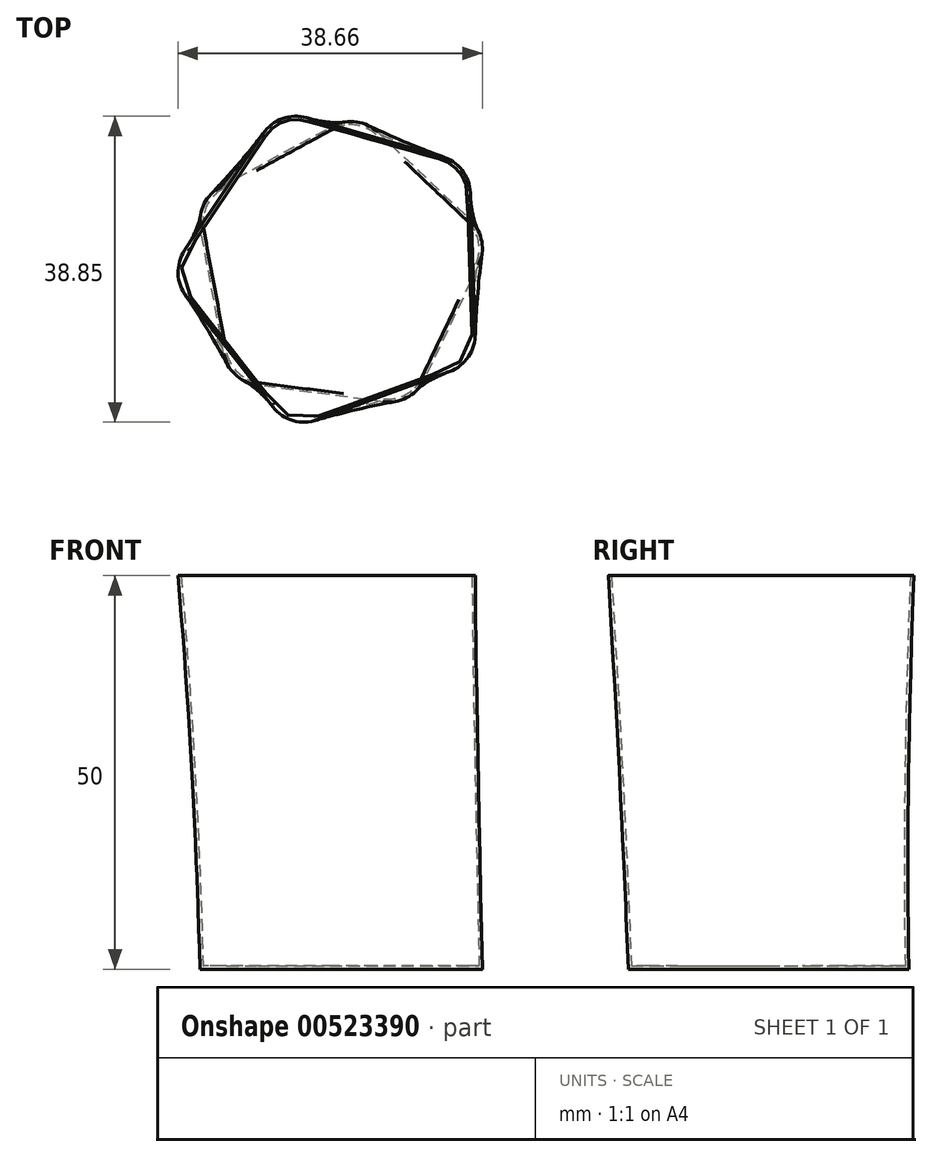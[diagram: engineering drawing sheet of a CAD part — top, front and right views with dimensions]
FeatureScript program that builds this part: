
annotation { "Feature Type Name" : "Feature", "Feature Type Description" : "" }
export const myFeature = defineFeature(function(context is Context, id is Id, definition is map)
    precondition{}
    {
        {
            var Q0;
            Q0=qCreatedBy(makeId("Top.planeOp"),FACE);
            var sketch = newSketch(context, id + "F0", { "sketchPlane" : qUnion([Q0])});
            skCircle(sketch, "E0.cCircle", {"center": v(0, 0) * mm, "radius": 16.1 * mm, "construction": true});
            skLineSegment(sketch, "E0.0", {"start": v(-14.77, 10.3) * mm, "end": v(-0.6, 18) * mm});
            skLineSegment(sketch, "E0.1", {"start": v(5.23, 17.23) * mm, "end": v(16.93, 6.13) * mm});
            skLineSegment(sketch, "E0.2", {"start": v(18, 0.35) * mm, "end": v(11.06, -14.2) * mm});
            skLineSegment(sketch, "E0.3", {"start": v(5.9, -17.01) * mm, "end": v(-10.1, -14.91) * mm});
            skLineSegment(sketch, "E0.4", {"start": v(-14.36, -10.87) * mm, "end": v(-17.3, 4.99) * mm});
            skPoint(sketch, "E0.0.midPoint", {"position": v(-7.69, 14.15) * mm});
            skPoint(sketch, "E1.visualSharp", {"position": v(2.6, 19.73) * mm});
            skArc(sketch, "E1.filletArc", {"start": v(5.23, 17.23) * mm, "mid": v(2.44, 18.56) * mm, "end": v(-0.6, 18) * mm});
            skPoint(sketch, "E2.visualSharp", {"position": v(19.56, 3.63) * mm});
            skArc(sketch, "E2.filletArc", {"start": v(18, 0.35) * mm, "mid": v(18.4, 3.42) * mm, "end": v(16.93, 6.13) * mm});
            skPoint(sketch, "E3.visualSharp", {"position": v(9.5, -17.48) * mm});
            skArc(sketch, "E3.filletArc", {"start": v(5.9, -17.01) * mm, "mid": v(8.94, -16.45) * mm, "end": v(11.06, -14.2) * mm});
            skPoint(sketch, "E4.visualSharp", {"position": v(-13.7, -14.44) * mm});
            skArc(sketch, "E4.filletArc", {"start": v(-14.36, -10.87) * mm, "mid": v(-12.88, -13.58) * mm, "end": v(-10.1, -14.91) * mm});
            skPoint(sketch, "E5.visualSharp", {"position": v(-17.96, 8.56) * mm});
            skArc(sketch, "E5.filletArc", {"start": v(-14.77, 10.3) * mm, "mid": v(-16.9, 8.05) * mm, "end": v(-17.3, 4.99) * mm});
            skSolve(sketch);
        }
        {
            var Q0;
            Q0=qCreatedBy(makeId("Top.planeOp"),FACE);
            cPlane(context, id + "F1", {"entities" : qUnion([Q0]), "cplaneType" : CPlaneType.OFFSET, "offset" : 50 * mm, "width" : 150 * mm, "height" : 150 * mm});
        }
        {
            var Q0;
            Q0=qCreatedBy(id+"F1.planeOp",FACE);
            var sketch = newSketch(context, id + "F2", { "sketchPlane" : qUnion([Q0])});
            skCircle(sketch, "E6.cCircle", {"center": v(0, 0) * mm, "radius": 17.28 * mm, "construction": true});
            skLineSegment(sketch, "E6.0", {"start": v(14.3, -13.18) * mm, "end": v(-2.46, -19.29) * mm});
            skLineSegment(sketch, "E6.1", {"start": v(-8.11, -17.67) * mm, "end": v(-19.1, -3.62) * mm});
            skLineSegment(sketch, "E6.2", {"start": v(-19.31, 2.26) * mm, "end": v(-9.34, 17.05) * mm});
            skLineSegment(sketch, "E6.3", {"start": v(-3.82, 19.06) * mm, "end": v(13.33, 14.16) * mm});
            skLineSegment(sketch, "E6.4", {"start": v(16.95, 9.53) * mm, "end": v(17.58, -8.3) * mm});
            skPoint(sketch, "E6.0.midPoint", {"position": v(5.92, -16.23) * mm});
            skPoint(sketch, "E7.visualSharp", {"position": v(-7.31, 20.06) * mm});
            skArc(sketch, "E7.filletArc", {"start": v(-3.82, 19.06) * mm, "mid": v(-6.91, 18.95) * mm, "end": v(-9.34, 17.05) * mm});
            skPoint(sketch, "E8.visualSharp", {"position": v(16.82, 13.16) * mm});
            skArc(sketch, "E8.filletArc", {"start": v(16.95, 9.53) * mm, "mid": v(15.9, 12.43) * mm, "end": v(13.33, 14.16) * mm});
            skPoint(sketch, "E9.visualSharp", {"position": v(17.71, -11.93) * mm});
            skArc(sketch, "E9.filletArc", {"start": v(14.3, -13.18) * mm, "mid": v(16.73, -11.27) * mm, "end": v(17.58, -8.3) * mm});
            skPoint(sketch, "E10.visualSharp", {"position": v(-5.88, -20.53) * mm});
            skArc(sketch, "E10.filletArc", {"start": v(-8.11, -17.67) * mm, "mid": v(-5.55, -19.4) * mm, "end": v(-2.46, -19.29) * mm});
            skPoint(sketch, "E11.visualSharp", {"position": v(-21.34, -0.76) * mm});
            skArc(sketch, "E11.filletArc", {"start": v(-19.31, 2.26) * mm, "mid": v(-20.16, -0.72) * mm, "end": v(-19.1, -3.62) * mm});
            skSolve(sketch);
        }
        {
            var Q0;
            Q0 = qSketchRegion(id + "F0", true);
            var Q1;
            Q1 = qSketchRegion(id + "F2", true);
            loft(context, id + "F3", {"sheetProfilesArray" : [{ "sheetProfileEntities" : qUnion([Q0]) }, { "sheetProfileEntities" : qUnion([Q1]) }]});
        }
        {
            var Q0;
            Q0=makeQuery(id+"F3.opLoft","CAP_FACE",FACE,{"disambiguationData":[OSD([makeQuery(id+"F2.imprint","IMPRINT",FACE,{"disambiguationData":[TD([[makeQuery(id+"F2.imprint","IMPRINT",EDGE,{"derivedFrom":sQuery(id+"F2.wireOp",EDGE,"E6.0")}),-1.0]])]})])],"isStart":true});
            shell(context, id + "F4", {"entities" : qUnion([Q0]), "thickness" : 0.4 * mm});
        }
    });
